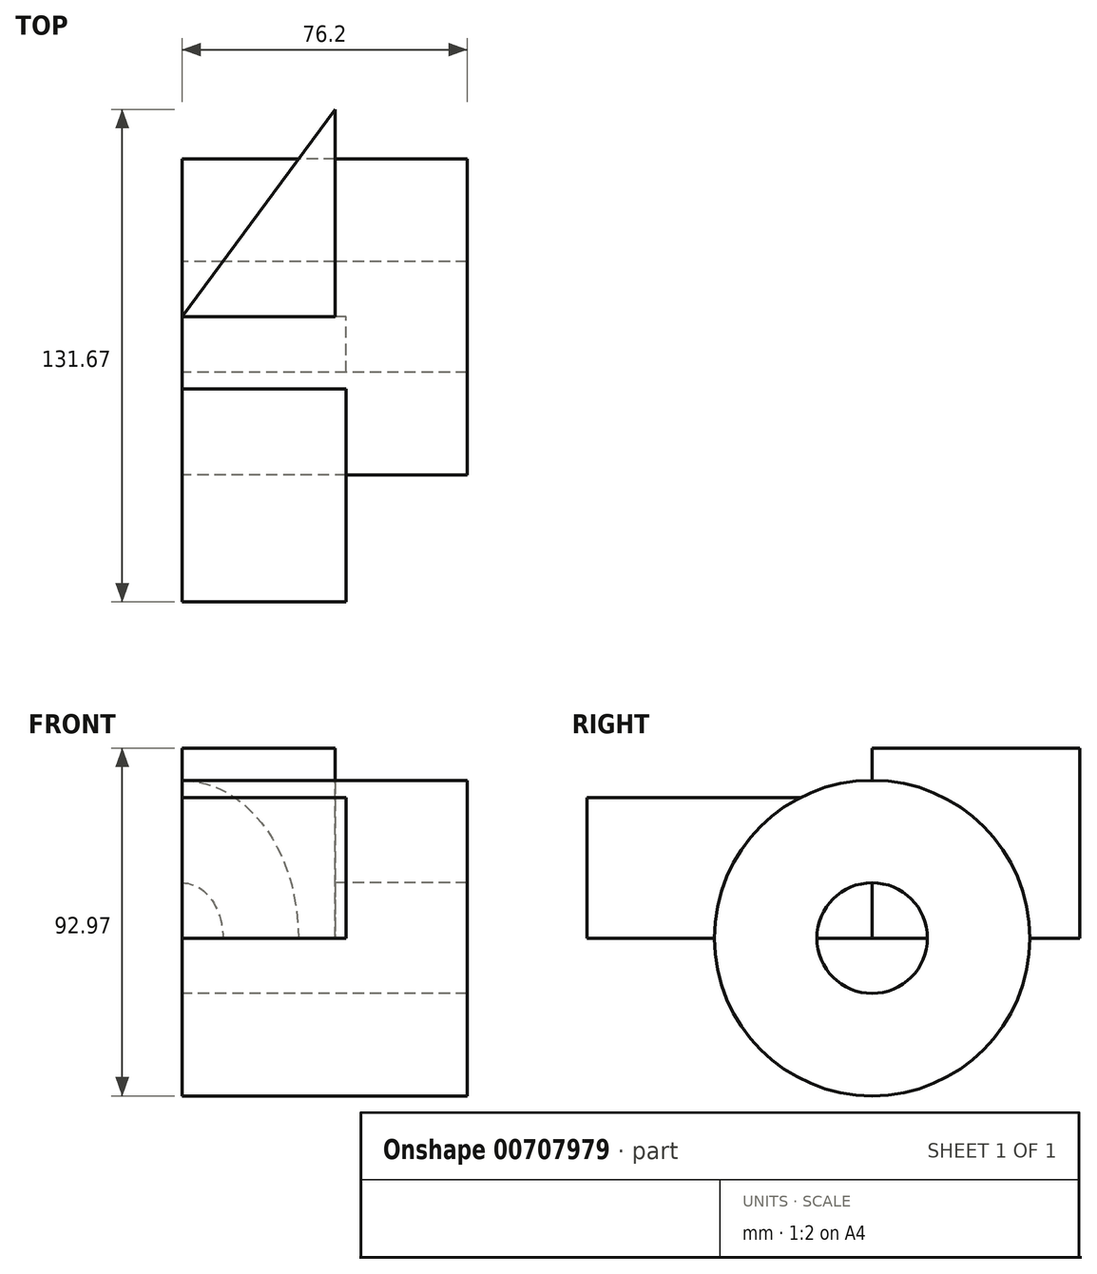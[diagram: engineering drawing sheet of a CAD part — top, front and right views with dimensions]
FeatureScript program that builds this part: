
annotation { "Feature Type Name" : "Feature", "Feature Type Description" : "" }
export const myFeature = defineFeature(function(context is Context, id is Id, definition is map)
    precondition{}
    {
        {
            var Q0;
            Q0=qCreatedBy(makeId("Front.planeOp"),FACE);
            var sketch = newSketch(context, id + "F0", { "sketchPlane" : qUnion([Q0])});
            skLineSegment(sketch, "E0.bottom", {"start": v(0, 0) * mm, "end": v(43.85, 0) * mm});
            skLineSegment(sketch, "E0.top", {"start": v(0, 37.54) * mm, "end": v(43.85, 37.54) * mm});
            skLineSegment(sketch, "E0.left", {"start": v(0, 0) * mm, "end": v(0, 37.54) * mm});
            skLineSegment(sketch, "E0.right", {"start": v(43.85, 0) * mm, "end": v(43.85, 37.54) * mm});
            skSolve(sketch);
        }
        {
            var Q0;
            Q0 = qSketchRegion(id + "F0", true);
            extrude(context, id + "F1", {"entities" : qUnion([Q0]), "depth" : 76.2 * mm, "offsetDistance" : 25.4 * mm});
        }
        {
            var Q0;
            Q0=qCreatedBy(makeId("Top.planeOp"),FACE);
            var sketch = newSketch(context, id + "F2", { "sketchPlane" : qUnion([Q0])});
            skLineSegment(sketch, "E1", {"start": v(0, 0) * mm, "end": v(40.9, 55.47) * mm});
            skLineSegment(sketch, "E2", {"start": v(40.9, 55.47) * mm, "end": v(40.9, 0) * mm});
            skLineSegment(sketch, "E3", {"start": v(40.9, 0) * mm, "end": v(0, 0) * mm});
            skSolve(sketch);
        }
        {
            var Q0;
            Q0=makeQuery(id+"F2.imprint","IMPRINT",FACE,{"disambiguationData":[TD([[makeQuery(id+"F2.imprint","IMPRINT",EDGE,{"derivedFrom":sQuery(id+"F2.wireOp",EDGE,"E1")}),-1.0]])]});
            extrude(context, id + "F3", {"entities" : qUnion([Q0]), "operationType" : NewBodyOperationType.ADD, "depth" : 50.8 * mm, "offsetDistance" : 25.4 * mm});
        }
        {
            var Q0;
            Q0=qCreatedBy(makeId("Right.planeOp"),FACE);
            var sketch = newSketch(context, id + "F4", { "sketchPlane" : qUnion([Q0])});
            skCircle(sketch, "E4", {"center": v(0, 0) * mm, "radius": 42.17 * mm});
            skCircle(sketch, "E5", {"center": v(0, 0) * mm, "radius": 14.78 * mm});
            skSolve(sketch);
        }
        {
            var Q0;
            Q0 = qSketchRegion(id + "F4", true);
            extrude(context, id + "F5", {"entities" : qUnion([Q0]), "operationType" : NewBodyOperationType.ADD, "depth" : 76.2 * mm, "offsetDistance" : 25.4 * mm});
        }
    });
